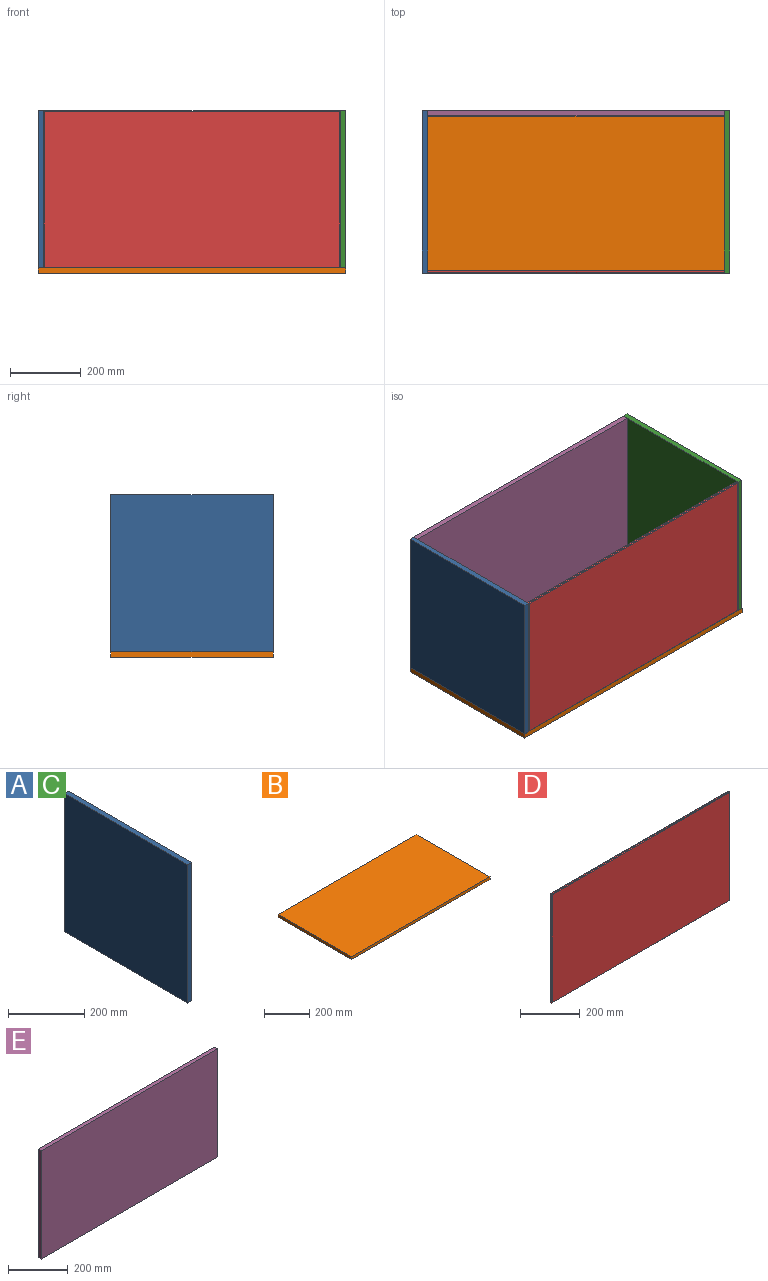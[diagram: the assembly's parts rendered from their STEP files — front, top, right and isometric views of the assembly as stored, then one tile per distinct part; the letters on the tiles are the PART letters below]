
ASSEMBLY  parts=5 mates=4
PART A: 6 faces, bbox 15x460x445 mm
  f0: plane 460x445mm, normal (1,0,0), area 204700mm2, adj f1,f3,f4,f5
  f1: plane 445x15mm, normal (0,1,0), area 6675mm2, adj f0,f2,f4,f5
  f2: plane 460x445mm, normal (-1,0,0), area 204700mm2, adj f1,f3,f4,f5
  f3: plane 445x15mm, normal (0,-1,0), area 6675mm2, adj f0,f2,f4,f5
  f4: plane 460x15mm, normal (0,0,1), area 6900mm2, adj f0,f1,f2,f3
  f5: plane 460x15mm, normal (0,0,-1), area 6900mm2, adj f0,f1,f2,f3
PART B: 6 faces, bbox 870x460x15 mm
  f0: plane 460x15mm, normal (1,0,0), area 6900mm2, adj f1,f3,f4,f5
  f1: plane 870x15mm, normal (0,1,0), area 13050mm2, adj f0,f2,f4,f5
  f2: plane 460x15mm, normal (-1,0,0), area 6900mm2, adj f1,f3,f4,f5
  f3: plane 870x15mm, normal (0,-1,0), area 13050mm2, adj f0,f2,f4,f5
  f4: plane 870x460mm, normal (0,0,1), area 400200mm2, adj f0,f1,f2,f3
  f5: plane 870x460mm, normal (0,0,-1), area 400200mm2, adj f0,f1,f2,f3
PART C: same geometry as A
PART D: 14 faces, bbox 840x8x445 mm
  f0: plane 445x4mm, normal (-1,0,0), area 1780mm2, adj f1,f3,f6,f10
  f1: plane 840x4mm, normal (0,0,-1), area 3360mm2, adj f0,f2,f7,f11
  f2: plane 445x4mm, normal (1,0,0), area 1780mm2, adj f1,f3,f9,f13
  f3: plane 840x4mm, normal (0,0,1), area 3360mm2, adj f0,f2,f8,f12
  f4: plane 836x441mm, normal (0,1,0), area 368676mm2, adj f6,f7,f8,f9
  f5: plane 836x441mm, normal (0,-1,0), area 368676mm2, adj f10,f11,f12,f13
  f6: plane 445x2mm, normal (-0.71,0.71,0), area 1253mm2, adj f0,f4,f7,f8
  f7: plane 840x2mm, normal (0,0.71,-0.71), area 2370.2mm2, adj f1,f4,f6,f9
  f8: plane 840x2mm, normal (0,0.71,0.71), area 2370.2mm2, adj f3,f4,f6,f9
  f9: plane 445x2mm, normal (0.71,0.71,0), area 1253mm2, adj f2,f4,f7,f8
  f10: plane 445x2mm, normal (-0.71,-0.71,0), area 1253mm2, adj f0,f5,f11,f12
  f11: plane 840x2mm, normal (0,-0.71,-0.71), area 2370.2mm2, adj f1,f5,f10,f13
  f12: plane 840x2mm, normal (0,-0.71,0.71), area 2370.2mm2, adj f3,f5,f10,f13
  f13: plane 445x2mm, normal (0.71,-0.71,0), area 1253mm2, adj f2,f5,f11,f12
PART E: 6 faces, bbox 840x15x445 mm
  f0: plane 445x15mm, normal (1,0,0), area 6675mm2, adj f1,f3,f4,f5
  f1: plane 840x15mm, normal (0,0,-1), area 12600mm2, adj f0,f2,f4,f5
  f2: plane 445x15mm, normal (-1,0,0), area 6675mm2, adj f1,f3,f4,f5
  f3: plane 840x15mm, normal (0,0,1), area 12600mm2, adj f0,f2,f4,f5
  f4: plane 840x445mm, normal (0,-1,0), area 373800mm2, adj f0,f1,f2,f3
  f5: plane 840x445mm, normal (0,1,0), area 373800mm2, adj f0,f1,f2,f3
PLACE A t=(-97.42,-29.23,105.29)mm
PLACE B t=(-97.42,-29.23,105.29)mm
PLACE C t=(757.58,-29.23,105.29)mm
PLACE D t=(-97.42,-29.23,105.29)mm
PLACE E t=(-97.42,-29.23,105.29)mm
MATE fastened D.f3 <-> A.f4  axis (0,0,1) through (-517.42,-259.23,565.29)mm
MATE fastened C.f0 <-> B.f0  axis (1,0,0) through (337.58,-259.23,120.29)mm
MATE fastened E.f3 <-> A.f4  axis (0,0,1) through (-517.42,200.77,565.29)mm
MATE fastened A.f5 <-> B.f4  axis (0,0,1) through (-532.42,-259.23,120.29)mm
